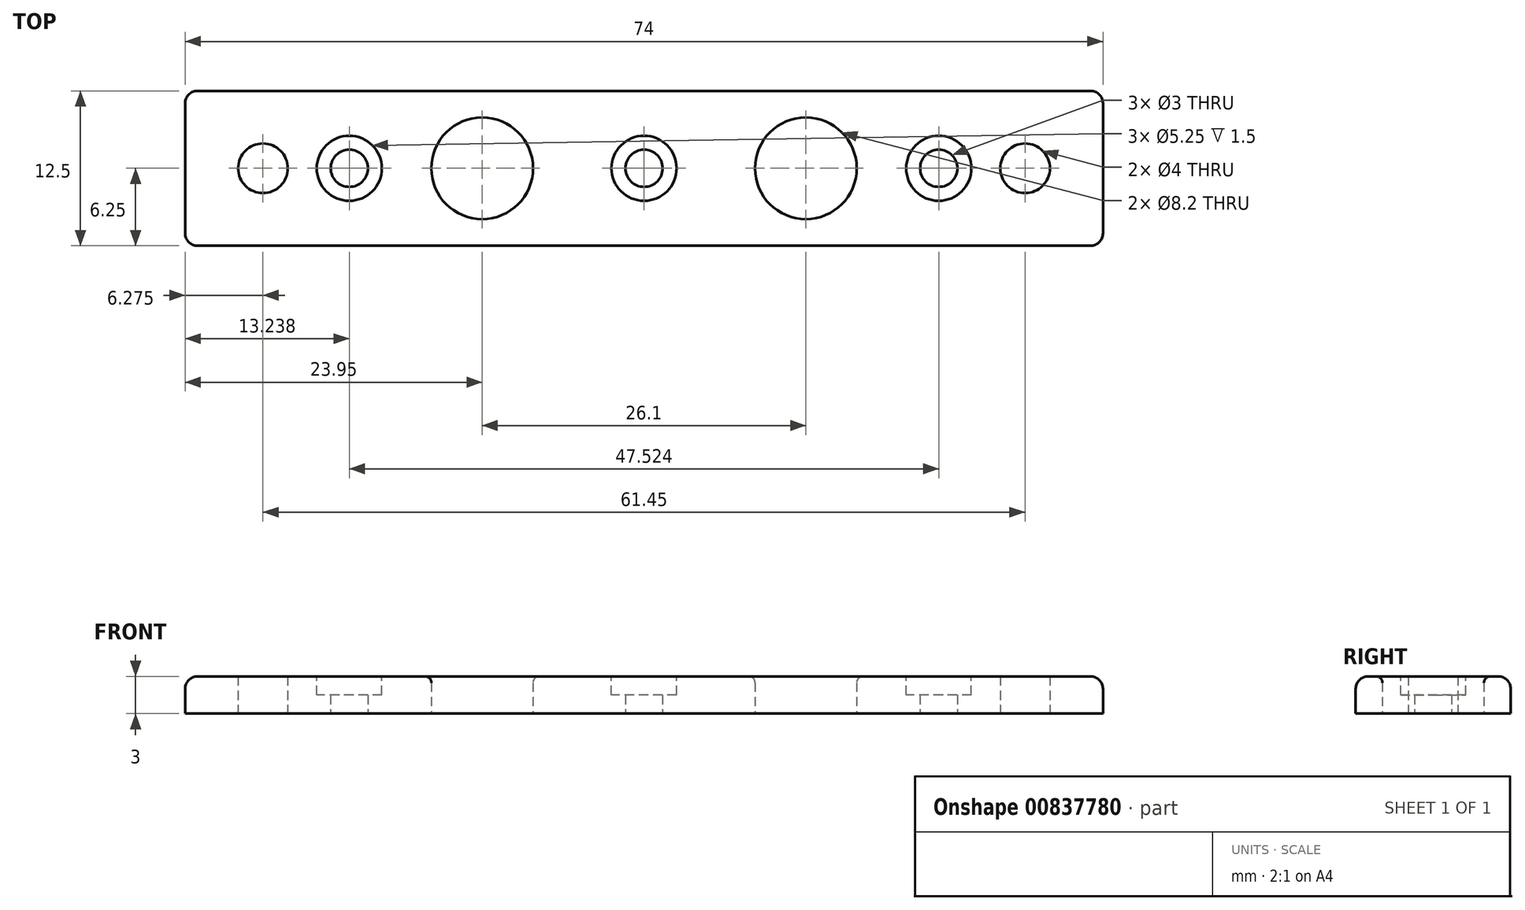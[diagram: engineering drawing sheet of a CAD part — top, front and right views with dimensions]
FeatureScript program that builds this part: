
annotation { "Feature Type Name" : "Feature", "Feature Type Description" : "" }
export const myFeature = defineFeature(function(context is Context, id is Id, definition is map)
    precondition{}
    {
        {
            var Q0;
            Q0=qCreatedBy(makeId("Top.planeOp"),FACE);
            var sketch = newSketch(context, id + "F0", { "sketchPlane" : qUnion([Q0])});
            skLineSegment(sketch, "E0.bottom", {"start": v(35, 6.25) * mm, "end": v(-35, 6.25) * mm});
            skLineSegment(sketch, "E0.top", {"start": v(35, -6.25) * mm, "end": v(-35, -6.25) * mm});
            skLineSegment(sketch, "E0.left", {"start": v(35, 6.25) * mm, "end": v(35, -6.25) * mm});
            skLineSegment(sketch, "E0.right", {"start": v(-35, 6.25) * mm, "end": v(-35, -6.25) * mm});
            skPoint(sketch, "E0.middle", {"position": v(0, 0) * mm});
            skCircle(sketch, "E1", {"center": v(0, 0) * mm, "radius": 1.5 * mm});
            skLineSegment(sketch, "E2", {"start": v(-35, 0) * mm, "end": v(-30.73, 0) * mm, "construction": true});
            skLineSegment(sketch, "E3", {"start": v(35, 0) * mm, "end": v(30.73, 0) * mm, "construction": true});
            skLineSegment(sketch, "E4", {"start": v(35, 0) * mm, "end": v(24.5, 0) * mm, "construction": true});
            skCircle(sketch, "E5", {"center": v(-30.73, 0) * mm, "radius": 2 * mm});
            skCircle(sketch, "E6", {"center": v(30.73, 0) * mm, "radius": 2 * mm});
            skLineSegment(sketch, "E7", {"start": v(35, 0) * mm, "end": v(13.05, 0) * mm, "construction": true});
            skCircle(sketch, "E8", {"center": v(-13.05, 0) * mm, "radius": 4.1 * mm});
            skCircle(sketch, "E9", {"center": v(13.05, 0) * mm, "radius": 4.1 * mm});
            skLineSegment(sketch, "E10", {"start": v(-35, 0) * mm, "end": v(-23.76, 0) * mm, "construction": true});
            skLineSegment(sketch, "E11", {"start": v(35, 0) * mm, "end": v(23.76, 0) * mm, "construction": true});
            skLineSegment(sketch, "E12", {"start": v(23.76, 0) * mm, "end": v(23.76, 1.32) * mm, "construction": true});
            skCircle(sketch, "E13", {"center": v(-23.76, 0) * mm, "radius": 1.5 * mm});
            skCircle(sketch, "E14", {"center": v(23.76, 0) * mm, "radius": 1.5 * mm});
            skLineSegment(sketch, "E15", {"start": v(-35, 6.25) * mm, "end": v(-37, 6.25) * mm});
            skLineSegment(sketch, "E16", {"start": v(-37, 6.25) * mm, "end": v(-37, -6.25) * mm});
            skLineSegment(sketch, "E17", {"start": v(-37, -6.25) * mm, "end": v(-35, -6.25) * mm});
            skLineSegment(sketch, "E18", {"start": v(35, 6.25) * mm, "end": v(37, 6.25) * mm});
            skLineSegment(sketch, "E19", {"start": v(37, 6.25) * mm, "end": v(37, -6.25) * mm});
            skLineSegment(sketch, "E20", {"start": v(37, -6.25) * mm, "end": v(35, -6.25) * mm});
            skSolve(sketch);
        }
        {
            var Q0;
            Q0 = qSketchRegion(id + "F0", true);
            extrude(context, id + "F1", {"entities" : qUnion([Q0]), "depth" : 3 * mm, "offsetDistance" : 25 * mm});
        }
        {
            var Q0;
            Q0=makeQuery(id+"F1.opExtrude","CAP_EDGE",EDGE,{"disambiguationData":[OSD([sQuery(id+"F0.wireOp",EDGE,"E8")])],"isStart":false});
            var Q1;
            Q1=makeQuery(id+"F1.opExtrude","CAP_EDGE",EDGE,{"disambiguationData":[OSD([sQuery(id+"F0.wireOp",EDGE,"E9")])],"isStart":false});
            fillet(context, id + "F2", {"entities" : qUnion([Q0, Q1]), "radius" : .5 * mm, "tangentPropagation" : true, "allowEdgeOverflow" : false});
        }
        {
            var Q0;
            Q0=makeQuery(id+"F1.opExtrude","CAP_FACE",FACE,{"disambiguationData":[OSD([sQuery(id+"F0.wireOp",EDGE,"E0.bottom"),sQuery(id+"F0.wireOp",EDGE,"E0.top"),sQuery(id+"F0.wireOp",EDGE,"E0.left"),sQuery(id+"F0.wireOp",EDGE,"E0.right"),sQuery(id+"F0.wireOp",EDGE,"E1"),sQuery(id+"F0.wireOp",EDGE,"E5"),sQuery(id+"F0.wireOp",EDGE,"E6"),sQuery(id+"F0.wireOp",EDGE,"E8"),sQuery(id+"F0.wireOp",EDGE,"E9"),sQuery(id+"F0.wireOp",EDGE,"E13"),sQuery(id+"F0.wireOp",EDGE,"E14")])],"isStart":false});
            var sketch = newSketch(context, id + "F3", { "sketchPlane" : qUnion([Q0])});
            skCircle(sketch, "E21", {"center": v(-23.76, 0) * mm, "radius": 2.62 * mm});
            skCircle(sketch, "E22", {"center": v(0, 0) * mm, "radius": 2.62 * mm});
            skCircle(sketch, "E23", {"center": v(23.76, 0) * mm, "radius": 2.62 * mm});
            skSolve(sketch);
        }
        {
            var Q0;
            Q0=makeQuery(id+"F3.imprint","IMPRINT",FACE,{"disambiguationData":[TD([[makeQuery(id+"F3.imprint","IMPRINT",EDGE,{"derivedFrom":sQuery(id+"F3.wireOp",EDGE,"E21")}),1.0]])]});
            var Q1;
            Q1=makeQuery(id+"F3.imprint","IMPRINT",FACE,{"disambiguationData":[TD([[makeQuery(id+"F3.imprint","IMPRINT",EDGE,{"derivedFrom":sQuery(id+"F3.wireOp",EDGE,"E22")}),1.0]])]});
            var Q2;
            Q2=makeQuery(id+"F3.imprint","IMPRINT",FACE,{"disambiguationData":[TD([[makeQuery(id+"F3.imprint","IMPRINT",EDGE,{"derivedFrom":sQuery(id+"F3.wireOp",EDGE,"E23")}),1.0]])]});
            extrude(context, id + "F4", {"entities" : qUnion([Q0, Q1, Q2]), "operationType" : NewBodyOperationType.REMOVE, "oppositeDirection" : true, "depth" : 1.5 * mm, "offsetDistance" : 25 * mm});
        }
        {
            var Q0;
            Q0=makeQuery(id+"F1.opExtrude","CAP_EDGE",EDGE,{"disambiguationData":[OSD([sQuery(id+"F0.wireOp",EDGE,"E0.bottom"),sQuery(id+"F0.wireOp",EDGE,"E15"),sQuery(id+"F0.wireOp",EDGE,"E18")])],"isStart":false});
            var Q1;
            Q1=makeQuery(id+"F1.opExtrude","CAP_EDGE",EDGE,{"disambiguationData":[OSD([sQuery(id+"F0.wireOp",EDGE,"E16")])],"isStart":false});
            var Q2;
            Q2=makeQuery(id+"F1.opExtrude","CAP_EDGE",EDGE,{"disambiguationData":[OSD([sQuery(id+"F0.wireOp",EDGE,"E0.top"),sQuery(id+"F0.wireOp",EDGE,"E17"),sQuery(id+"F0.wireOp",EDGE,"E20")])],"isStart":false});
            var Q3;
            Q3=makeQuery(id+"F1.opExtrude","CAP_EDGE",EDGE,{"disambiguationData":[OSD([sQuery(id+"F0.wireOp",EDGE,"E19")])],"isStart":false});
            var Q4;
            Q4=makeQuery(id+"F1.opExtrude","SWEPT_EDGE",EDGE,{"disambiguationData":[OSD([sQuery(id+"F0.wireOp",EDGE,"E15"),sQuery(id+"F0.wireOp",EDGE,"E16")])]});
            var Q5;
            Q5=makeQuery(id+"F1.opExtrude","SWEPT_EDGE",EDGE,{"disambiguationData":[OSD([sQuery(id+"F0.wireOp",EDGE,"E16"),sQuery(id+"F0.wireOp",EDGE,"E17")])]});
            var Q6;
            Q6=makeQuery(id+"F1.opExtrude","SWEPT_EDGE",EDGE,{"disambiguationData":[OSD([sQuery(id+"F0.wireOp",EDGE,"E18"),sQuery(id+"F0.wireOp",EDGE,"E19")])]});
            var Q7;
            Q7=makeQuery(id+"F1.opExtrude","SWEPT_EDGE",EDGE,{"disambiguationData":[OSD([sQuery(id+"F0.wireOp",EDGE,"E19"),sQuery(id+"F0.wireOp",EDGE,"E20")])]});
            fillet(context, id + "F5", {"entities" : qUnion([Q0, Q1, Q2, Q3, Q4, Q5, Q6, Q7]), "radius" : 1 * mm, "tangentPropagation" : true, "allowEdgeOverflow" : false});
        }
    });
